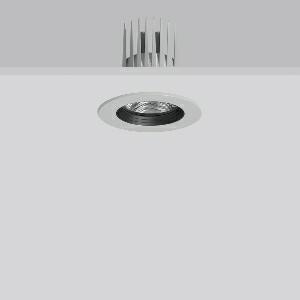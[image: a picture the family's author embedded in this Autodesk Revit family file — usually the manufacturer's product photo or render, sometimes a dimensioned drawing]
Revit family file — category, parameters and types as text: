
# Revit family: heledon_mini_e_901750_004_1_76_a3d0
name_source: partatom
category: Lighting Fixtures
units: mm (PartAtom-declared; Revit-internal decimal feet)

## family parameters
Cut with Voids When Loaded = No
Host = Face
Light Source = No
Part Type = Normal
Room Calculation Point = No
Round Connector Dimension = Use Diameter
Shared = No

## types (1)
- HELEDON mini E (1 x LED Modul 940, 3900 lm, 4000)
    Apparent Load = 29 VA
    Approval mark = CE
    CIE Flux Codes = 95 99 100 100 100
    Color Rendering = 92
    Color Temperature = 4000
    Default Elevation = 1800 mm
    Description = Series: HELEDON mini
Round recessed downlight. Housing: die-cast aluminium, powder-coated. Black plastic ring and recessed LED to prevent glare from the side. Optical assembly with reflector made of MIRO-Silver with 98% total light reflection for outstanding efficiency - can be changed without tools. Best colour rendering index Ra>90. Suitable for Recessed ceiling mounting. Installation without tools thanks to spring fastening system. Including separate LED converter with connecting cable 600 mm.High quality converter without flickering and stroboscopic effect. Through-wiring box (5 pole) available as accessory. The following accessories can be mounted without use of tools: interchangeable lenses, decorative glasses, honeycomb louvre, clear and frosted diffusers, white interchangeable plastic ring. 
Colour: silver
Diameter: 124 mm
Height: 3 mm
Cut-out diameter: 114 mm
Recess height: 170 mm
Luminaire: recess height: 120 mm
Lamp: LED
Socket: without socket
Colour temperature: 4000K
Colour rendering index (CRI): 92
System power: 29 W
Rated luminous flux: 3900 lm
Luminous efficiency: 134 lm/W
Control gear: Converter, dimmable, DALI
Protection class: II
Type of protection: IP 20
    Height = 0 mm  [stored 0 ft]
    Lamp = 1 x LED Modul 940
    Lamp Light Flux = 3900 lm
    Lamp count = 1
    Length = 124 mm  [stored 0.406824 ft]
    Lifetime = 50000 h
    Luminous efficacy = 134 lm/W
    Manufacturer = RZB
    ModVariant = No
    Model = 901750.004.1.76
    Mounting Place = Ceiling
    Mounting Type = Recessed
    Number of Poles = 1
    OnlyDefault = Yes
    Power Factor = 1
    Product Name = HELEDON mini E
    Product group = Recessed downlights
    ProductGroupID = 402
    Protection Class = Protection class II
    Protection Degree = IP 20
    RLX_Detail_Level = 1
    RLX_Emergency_Light_Flux = 0 lm
    RLX_Emergency_Type = 0
    RLX_Emergency_Type_DB = No
    RlxData = <blob elided: 126969 chars, md5=d2ff6b1e>
    Socket = socket
    Standby Power = 0 W
    System Light Flux = 3900 lm
    System Power = 29 W
    Type Comments = Product without accessories
    Type Image = 901657.004.jpg
    URL = http://relux.com
    VarID = ---
    Voltage = 230 V
    Voltage Range = 220-240 V
    Weight = 0.00 kg
    Width = 0 mm  [stored 0 ft]

note: [stored X ft] marks values corroborated as IEEE doubles in the binary element streams (Revit-internal decimal feet)

## geometry (parser evidence)
native form markers: Blend x4, Sweep x12
no freeform markers — native parametric forms only
